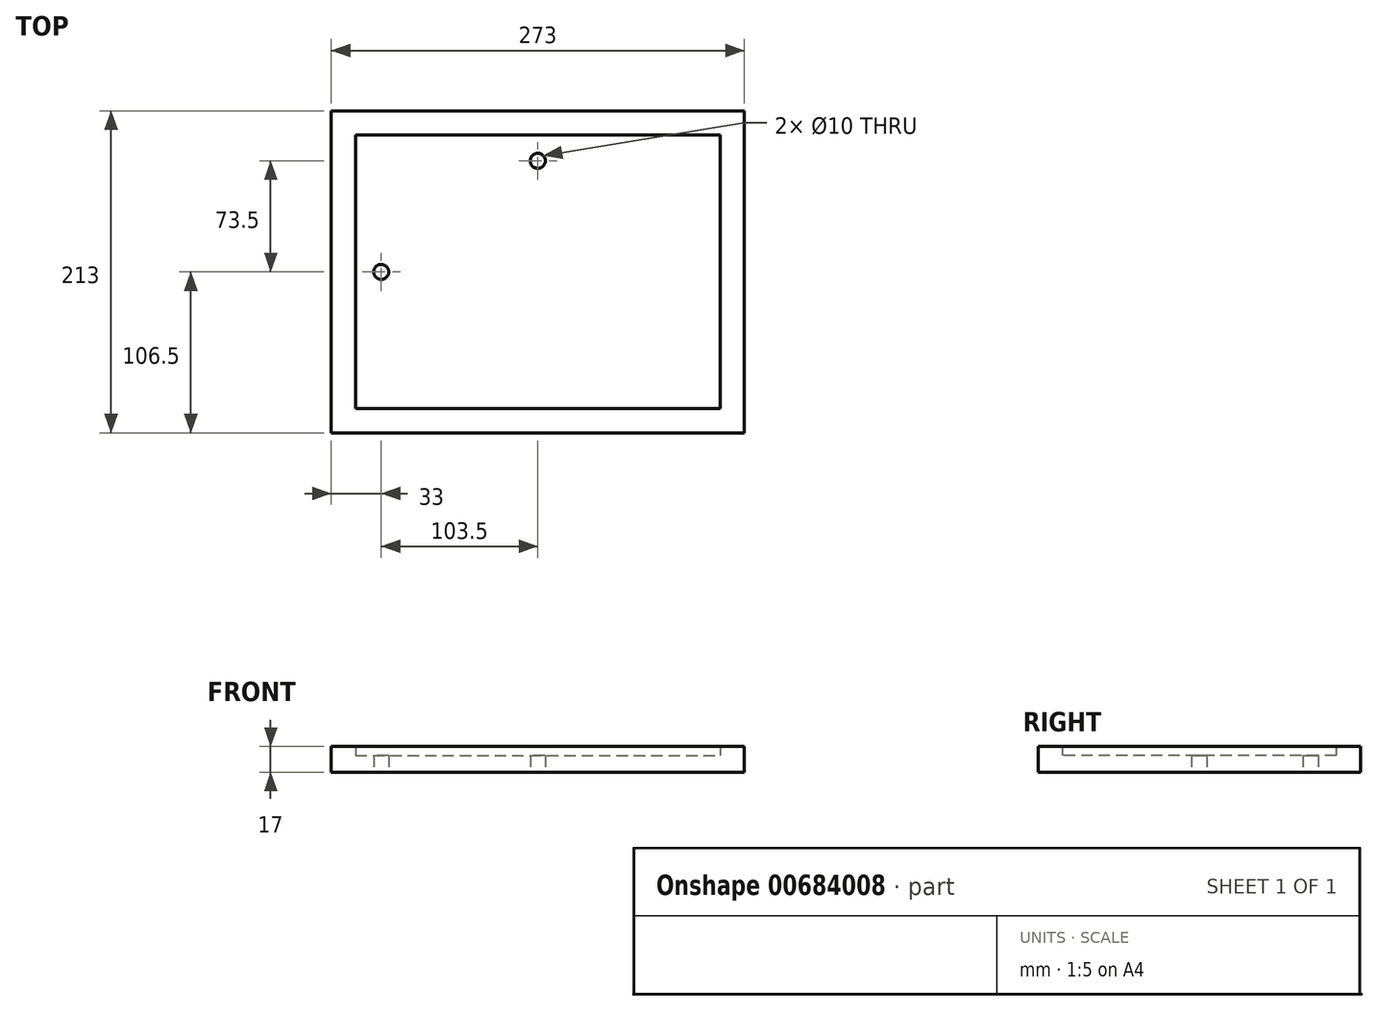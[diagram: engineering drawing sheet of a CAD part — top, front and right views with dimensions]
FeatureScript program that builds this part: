
annotation { "Feature Type Name" : "Feature", "Feature Type Description" : "" }
export const myFeature = defineFeature(function(context is Context, id is Id, definition is map)
    precondition{}
    {
        {
            var Q0;
            Q0=qCreatedBy(makeId("Top.planeOp"),FACE);
            var sketch = newSketch(context, id + "F0", { "sketchPlane" : qUnion([Q0])});
            skLineSegment(sketch, "E0.bottom", {"start": v(-136.5, 106.5) * mm, "end": v(136.5, 106.5) * mm});
            skLineSegment(sketch, "E0.top", {"start": v(-136.5, -106.5) * mm, "end": v(136.5, -106.5) * mm});
            skLineSegment(sketch, "E0.left", {"start": v(-136.5, 106.5) * mm, "end": v(-136.5, -106.5) * mm});
            skLineSegment(sketch, "E0.right", {"start": v(136.5, 106.5) * mm, "end": v(136.5, -106.5) * mm});
            skCircle(sketch, "E1", {"center": v(-103.5, 0) * mm, "radius": 5 * mm});
            skCircle(sketch, "E2", {"center": v(0, 73.5) * mm, "radius": 5 * mm});
            skLineSegment(sketch, "E3", {"start": v(0, 106.5) * mm, "end": v(0, -106.5) * mm, "construction": true});
            skLineSegment(sketch, "E4", {"start": v(0, -106.5) * mm, "end": v(136.5, 0) * mm, "construction": true});
            skLineSegment(sketch, "E5", {"start": v(136.5, 0) * mm, "end": v(-136.5, 0) * mm, "construction": true});
            skLineSegment(sketch, "E6.0", {"start": v(-120.5, -90.5) * mm, "end": v(120.5, -90.5) * mm});
            skLineSegment(sketch, "E6.1", {"start": v(-120.5, 90.5) * mm, "end": v(-120.5, -90.5) * mm});
            skLineSegment(sketch, "E6.2", {"start": v(-120.5, 90.5) * mm, "end": v(120.5, 90.5) * mm});
            skLineSegment(sketch, "E6.3", {"start": v(120.5, 90.5) * mm, "end": v(120.5, -90.5) * mm});
            skSolve(sketch);
        }
        {
            var Q0;
            Q0=makeQuery(id+"F0.imprint","IMPRINT",FACE,{"disambiguationData":[TD([[makeQuery(id+"F0.imprint","IMPRINT",EDGE,{"derivedFrom":sQuery(id+"F0.wireOp",EDGE,"E0.bottom")}),-1.0]])]});
            extrude(context, id + "F1", {"entities" : qUnion([Q0]), "depth" : 17 * mm, "offsetDistance" : 25 * mm});
        }
        {
            var Q0;
            Q0=makeQuery(id+"F0.imprint","IMPRINT",FACE,{"disambiguationData":[TD([[makeQuery(id+"F0.imprint","IMPRINT",EDGE,{"derivedFrom":sQuery(id+"F0.wireOp",EDGE,"E1")}),-1.0]])]});
            extrude(context, id + "F2", {"entities" : qUnion([Q0]), "operationType" : NewBodyOperationType.ADD, "depth" : 11 * mm, "offsetDistance" : 25 * mm});
        }
    });
